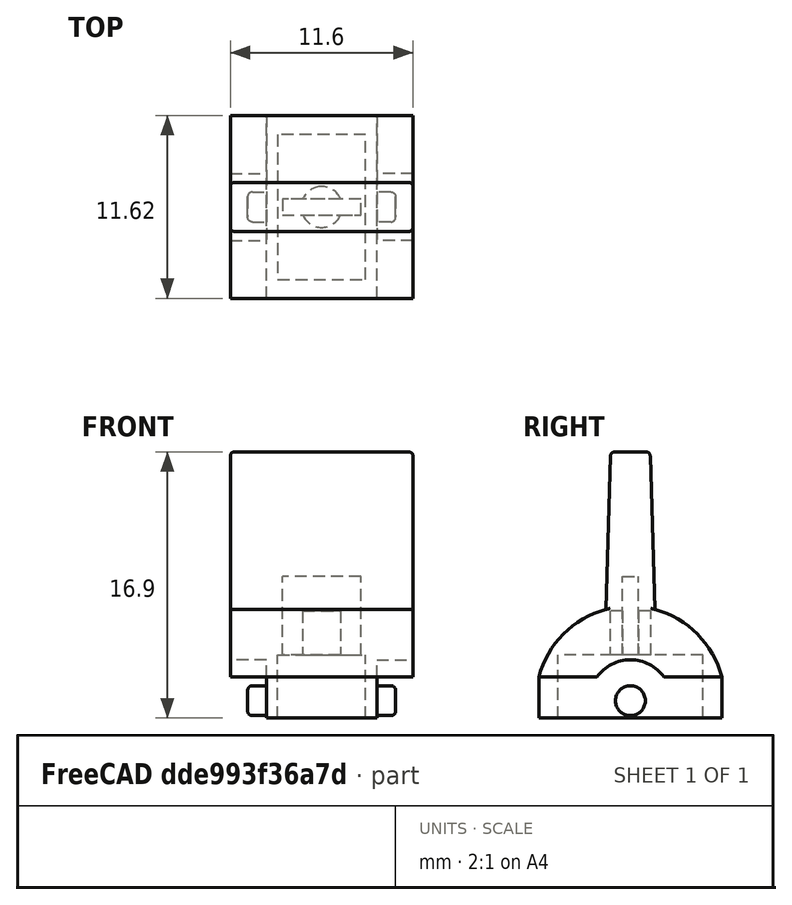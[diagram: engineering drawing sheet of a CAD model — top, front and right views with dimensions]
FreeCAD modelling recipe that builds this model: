
FCSTD DOCUMENT  (FreeCAD 0.21R33771 (Git))
Label: switch lever 
License: All rights reserved
LicenseURL: http://en.wikipedia.org/wiki/All_rights_reserved
objects: Sketcher::SketchObject×6, PartDesign::Pocket×4, PartDesign::Pad×2, PartDesign::Mirrored×2, PartDesign::Fillet×2, PartDesign::Body×1, Mesh::Feature×1
note: 25 computed .brp shape members not serialized (recipe doc carries the construction recipe); baked Part::Feature solids carry a one-line shape summary decoded from their .brp

FEATURE [Sketcher::SketchObject] Sketch
  FullyConstrained = true
  MapMode = 5
  Support = -> [XY_Plane]
  sketch-geometry (8):
    g0: LineSegment StartX=-15.7963 StartY=1.25 StartZ=0 EndX=-15.7963 EndY=-1.25 EndZ=0
    g1: LineSegment StartX=-15.7963 StartY=-1.25 StartZ=0 EndX=-5.79634 EndY=-1.55 EndZ=0
    g2: LineSegment StartX=-15.7963 StartY=1.25 StartZ=0 EndX=-5.79634 EndY=1.55 EndZ=0
    g3: ArcOfCircle CenterX=0 CenterY=0 CenterZ=0 NormalX=0 NormalY=0 NormalZ=1 AngleXU=0 Radius=6 StartAngle=1.82348 EndAngle=2.8803
    g4: ArcOfCircle CenterX=0 CenterY=0 CenterZ=0 NormalX=0 NormalY=0 NormalZ=1 AngleXU=0 Radius=6 StartAngle=3.40289 EndAngle=4.45971
    g5: LineSegment StartX=-1.5 StartY=5.80948 StartZ=0 EndX=1.1 EndY=5.80948 EndZ=0
    g6: LineSegment StartX=1.1 StartY=5.80948 StartZ=0 EndX=1.1 EndY=-5.80948 EndZ=0
    g7: LineSegment StartX=1.1 StartY=-5.80948 StartZ=0 EndX=-1.5 EndY=-5.80948 EndZ=0
  constraints (22):
    c: Coincident(g0,g1)
    c: Coincident(g0,g2)
    c: Coincident(g3,g-1)
    c: Coincident(g3,g2)
    c: Coincident(g4,g3)
    c: Coincident(g4,g1)
    c: Symmetric(g2,g1,g-1)
    c: Symmetric(g0,g0,g-1)
    c: Radius(g3) = 6
    c: Coincident(g5,g6)
    c: Vertical(g6)
    c: Coincident(g6,g7)
    c: Coincident(g7,g4)
    c: Horizontal(g5)
    c: Horizontal(g7)
    c: Coincident(g5,g3)
    c: Vertical(g4,g3)
    c: DistanceX(g3,g-1) = 1.5
    c: DistanceX(g5,g5) = 2.6
    c: DistanceX(g2,g2) = 10
    c: DistanceY(g1,g2) = 3.1
    c: DistanceY(g0,g0) = 2.5
FEATURE [PartDesign::Pad] Pad
  Direction = (0,0,1)
  Length = 11.6
  Length2 = 10
  Midplane = true
  Profile = -> Sketch
  ReferenceAxis = -> Sketch [N_Axis]
  Type = 0
FEATURE [Sketcher::SketchObject] Sketch001
  ExternalGeometry = -> [Pad]
  FullyConstrained = false
  MapMode = 5
  Placement = pos=(0,0,5.8) rot=(0,0,1;0rad)
  Support = -> [Pad]
  sketch-geometry (6):
    g0: ArcOfCircle CenterX=0 CenterY=0 CenterZ=0 NormalX=0 NormalY=0 NormalZ=1 AngleXU=0 Radius=2.6 StartAngle=2.18575 EndAngle=4.09743
    g1: LineSegment StartX=-1.5 StartY=-5.80948 StartZ=0 EndX=-1.5 EndY=-2.12368 EndZ=0
    g2: LineSegment StartX=-1.5 StartY=-5.80948 StartZ=0 EndX=1.1 EndY=-5.80948 EndZ=0
    g3: LineSegment StartX=1.1 StartY=-5.80948 StartZ=0 EndX=1.1 EndY=5.80948 EndZ=0
    g4: LineSegment StartX=1.1 StartY=5.80948 StartZ=0 EndX=-1.5 EndY=5.80948 EndZ=0
    g5: LineSegment StartX=-1.5 StartY=5.80948 StartZ=0 EndX=-1.5 EndY=2.12368 EndZ=0
  constraints (15):
    c: DistanceX(g0,g-3) = 2.6
    c: Vertical(g0,g0)
    c: Radius(g0) = 2.6
    c: PointOnObject(g1,g-5)
    c: Vertical(g1)
    c: Coincident(g1,g2)
    c: Coincident(g2,g-5)
    c: Coincident(g2,g3)
    c: Coincident(g3,g-4)
    c: Coincident(g3,g4)
    c: PointOnObject(g4,g-4)
    c: Coincident(g4,g5)
    c: Vertical(g5)
    c: Coincident(g5,g0)
    c: Coincident(g1,g0)
FEATURE [PartDesign::Pocket] Pocket
  BaseFeature = -> Pad
  Direction = (0,0,-1)
  Length = 2.3
  Length2 = 5
  Profile = -> Sketch001
  ReferenceAxis = -> Sketch001 [N_Axis]
  Type = 0
FEATURE [PartDesign::Mirrored] Mirrored
  BaseFeature = -> Pocket
  MirrorPlane = -> XY_Plane
  Originals = -> [Pocket]
FEATURE [Sketcher::SketchObject] Sketch002
  FullyConstrained = true
  MapMode = 5
  Placement = pos=(0,0,3.5) rot=(0,0,1;0rad)
  Support = -> [Mirrored]
  sketch-geometry (1):
    g0: Circle CenterX=0 CenterY=0 CenterZ=0 NormalX=0 NormalY=0 NormalZ=1 AngleXU=0 Radius=0.95
  constraints (2):
    c: Coincident(g0,g-1)
    c: Diameter(g0) = 1.9
FEATURE [PartDesign::Pad] Pad001
  BaseFeature = -> Mirrored
  Direction = (0,0,1)
  Length = 1.2
  Length2 = 10
  Profile = -> Sketch002
  ReferenceAxis = -> Sketch002 [N_Axis]
  Type = 0
FEATURE [PartDesign::Mirrored] Mirrored001
  BaseFeature = -> Pad001
  MirrorPlane = -> XY_Plane
  Originals = -> [Pad001]
FEATURE [Sketcher::SketchObject] Sketch003
  FullyConstrained = true
  MapMode = 5
  Placement = pos=(1.1,0,0) rot=(0.57735,0.57735,0.57735;2.0944rad)
  Support = -> [Mirrored001]
  sketch-geometry (4):
    g0: LineSegment StartX=-4.6 StartY=2.8 StartZ=0 EndX=4.6 EndY=2.8 EndZ=0
    g1: LineSegment StartX=4.6 StartY=2.8 StartZ=0 EndX=4.6 EndY=-2.8 EndZ=0
    g2: LineSegment StartX=4.6 StartY=-2.8 StartZ=0 EndX=-4.6 EndY=-2.8 EndZ=0
    g3: LineSegment StartX=-4.6 StartY=-2.8 StartZ=0 EndX=-4.6 EndY=2.8 EndZ=0
  constraints (11):
    c: Coincident(g0,g1)
    c: Coincident(g1,g2)
    c: Coincident(g2,g3)
    c: Coincident(g3,g0)
    c: Horizontal(g0)
    c: Horizontal(g2)
    c: Vertical(g1)
    c: Vertical(g3)
    c: Symmetric(g0,g2,g-1)
    c: DistanceY(g3,g3) = 5.6
    c: DistanceX(g0,g0) = 9.2
FEATURE [PartDesign::Pocket] Pocket001
  BaseFeature = -> Mirrored001
  Direction = (-1,0,0)
  Length = 4
  Length2 = 5
  Profile = -> Sketch003
  ReferenceAxis = -> Sketch003 [N_Axis]
  Type = 0
FEATURE [Sketcher::SketchObject] Sketch004
  FullyConstrained = true
  MapMode = 5
  Placement = pos=(-2.9,0,0) rot=(0.57735,0.57735,0.57735;2.0944rad)
  Support = -> [Pocket001]
  sketch-geometry (1):
    g0: Circle CenterX=0 CenterY=0 CenterZ=0 NormalX=0 NormalY=0 NormalZ=1 AngleXU=0 Radius=1.3
  constraints (2):
    c: Coincident(g0,g-1)
    c: Diameter(g0) = 2.6
FEATURE [PartDesign::Pocket] Pocket002
  BaseFeature = -> Pocket001
  Direction = (-1,0,0)
  Length = 2.8
  Length2 = 5
  Profile = -> Sketch004
  ReferenceAxis = -> Sketch004 [N_Axis]
  Type = 0
FEATURE [Sketcher::SketchObject] Sketch005
  FullyConstrained = true
  MapMode = 5
  Placement = pos=(-2.9,0,0) rot=(0.57735,0.57735,0.57735;2.0944rad)
  Support = -> [Pocket002]
  sketch-geometry (4):
    g0: LineSegment StartX=-0.5 StartY=2.5 StartZ=0 EndX=0.5 EndY=2.5 EndZ=0
    g1: LineSegment StartX=0.5 StartY=2.5 StartZ=0 EndX=0.5 EndY=-2.5 EndZ=0
    g2: LineSegment StartX=0.5 StartY=-2.5 StartZ=0 EndX=-0.5 EndY=-2.5 EndZ=0
    g3: LineSegment StartX=-0.5 StartY=-2.5 StartZ=0 EndX=-0.5 EndY=2.5 EndZ=0
  constraints (11):
    c: Coincident(g0,g1)
    c: Coincident(g1,g2)
    c: Coincident(g2,g3)
    c: Coincident(g3,g0)
    c: Horizontal(g0)
    c: Horizontal(g2)
    c: Vertical(g1)
    c: Vertical(g3)
    c: Symmetric(g0,g2,g-1)
    c: DistanceX(g0,g0) = 1
    c: DistanceY(g1,g1) = 5
FEATURE [PartDesign::Pocket] Pocket003
  BaseFeature = -> Pocket002
  Direction = (-1,0,0)
  Length = 5
  Length2 = 5
  Profile = -> Sketch005
  ReferenceAxis = -> Sketch005 [N_Axis]
  Type = 0
FEATURE [PartDesign::Fillet] Fillet
  Base = -> Pocket003 [Edge52,Edge54]
  BaseFeature = -> Pocket003
  Radius = 0.3
  SupportTransform = false
  UseAllEdges = false
FEATURE [PartDesign::Fillet] Fillet001
  Base = -> Fillet [Edge30,Edge33,Edge34,Edge55,Edge56,Edge54,Edge57,Edge53]
  BaseFeature = -> Fillet
  Radius = 0.25
  SupportTransform = false
  UseAllEdges = false
FEATURE [PartDesign::Body] Body
  Group = -> [Sketch,Pad,Sketch001,Pocket,Mirrored,Sketch002,Pad001,Mirrored001,Sketch003,Pocket001,Sketch004,Pocket002,Sketch005,Pocket003,Fillet,Fillet001]
  Origin = -> Origin
  Placement = pos=(0,0,0) rot=(0,1,0;1.5708rad)
  Tip = -> Fillet001
FEATURE [Mesh::Feature] Mesh  label="Body (Meshed)"
